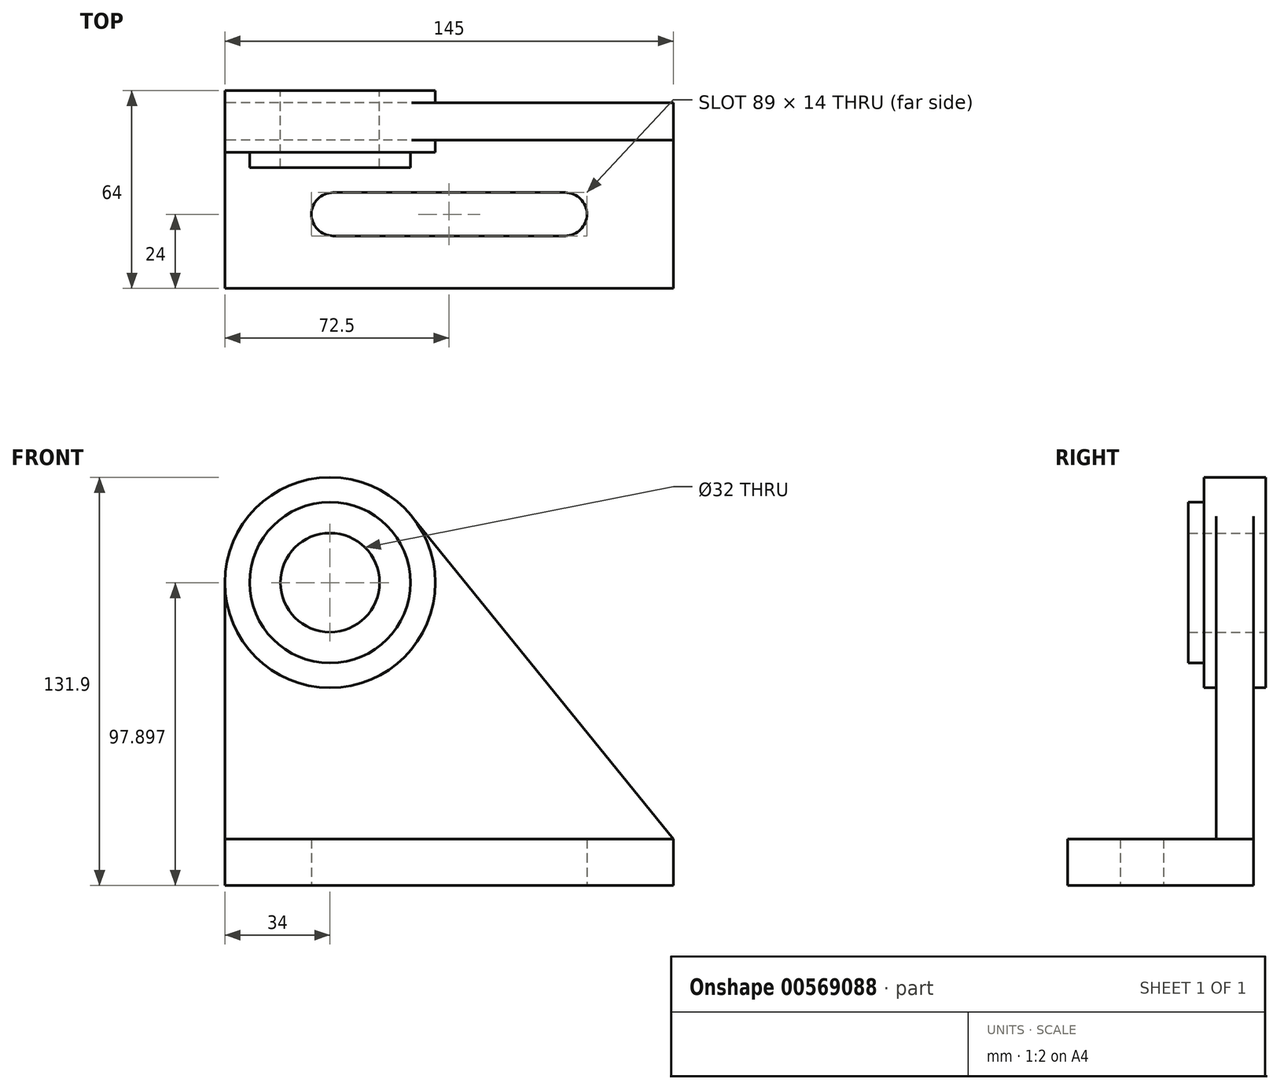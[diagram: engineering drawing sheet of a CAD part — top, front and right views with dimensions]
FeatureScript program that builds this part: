
annotation { "Feature Type Name" : "Feature", "Feature Type Description" : "" }
export const myFeature = defineFeature(function(context is Context, id is Id, definition is map)
    precondition{}
    {
        {
            var Q0;
            Q0=qCreatedBy(makeId("Top.planeOp"),FACE);
            var sketch = newSketch(context, id + "F0", { "sketchPlane" : qUnion([Q0])});
            skLineSegment(sketch, "E0.bottom", {"start": v(-72.5, 30) * mm, "end": v(72.5, 30) * mm});
            skLineSegment(sketch, "E0.top", {"start": v(-72.5, -30) * mm, "end": v(72.5, -30) * mm});
            skLineSegment(sketch, "E0.left", {"start": v(-72.5, 30) * mm, "end": v(-72.5, -30) * mm});
            skLineSegment(sketch, "E0.right", {"start": v(72.5, 30) * mm, "end": v(72.5, -30) * mm});
            skArc(sketch, "E1", {"start": v(37.5, -13) * mm, "mid": v(44.5, -6) * mm, "end": v(37.5, 1) * mm});
            skArc(sketch, "E2", {"start": v(-37.5, 1) * mm, "mid": v(-44.5, -6) * mm, "end": v(-37.5, -13) * mm});
            skLineSegment(sketch, "E3", {"start": v(-37.5, 1) * mm, "end": v(37.5, 1) * mm});
            skLineSegment(sketch, "E4", {"start": v(-37.5, -13) * mm, "end": v(37.5, -13) * mm});
            skSolve(sketch);
        }
        {
            var Q0;
            Q0=qSketchRegion(id+"F0",true);
            extrude(context, id + "F1", {"entities" : qUnion([Q0]), "depth" : 15 * mm});
        }
        {
            var Q0;
            Q0=makeQuery(id+"F1.opExtrude","SWEPT_FACE",FACE,{"disambiguationData":[OSD([sQuery(id+"F0.wireOp",EDGE,"E0.bottom")])]});
            cPlane(context, id + "F2", {"entities" : qUnion([Q0]), "cplaneType" : CPlaneType.OFFSET, "offset" : 0 * mm, "width" : 150 * mm, "height" : 150 * mm});
        }
        {
            var Q0;
            Q0=qCreatedBy(id+"F2.planeOp",FACE);
            var sketch = newSketch(context, id + "F3", { "sketchPlane" : qUnion([Q0])});
            skLineSegment(sketch, "E5.bottom", {"start": v(-72.5, 15) * mm, "end": v(72.5, 15) * mm});
            skLineSegment(sketch, "E5.top", {"start": v(-72.5, 0) * mm, "end": v(72.5, 0) * mm});
            skLineSegment(sketch, "E5.left", {"start": v(-72.5, 15) * mm, "end": v(-72.5, 0) * mm});
            skLineSegment(sketch, "E5.right", {"start": v(72.5, 15) * mm, "end": v(72.5, 0) * mm});
            skLineSegment(sketch, "E6", {"start": v(72.5, 15) * mm, "end": v(72.5, 103.43) * mm});
            skCircle(sketch, "E7", {"center": v(38.5, 97.9) * mm, "radius": 16 * mm});
            skCircle(sketch, "E8", {"center": v(38.5, 97.9) * mm, "radius": 26 * mm});
            skCircle(sketch, "E9", {"center": v(38.5, 97.9) * mm, "radius": 34 * mm});
            skLineSegment(sketch, "E10", {"start": v(-72.5, 15) * mm, "end": v(12.1, 119.31) * mm});
            skSolve(sketch);
        }
        {
            var Q0;
            {var subQ0=sQuery(id+"F3.wireOp",EDGE,"E5.bottom");Q0=makeQuery(id+"F3.imprint","IMPRINT",FACE,{"disambiguationData":[TD([[makeQuery(id+"F3.imprint","IMPRINT",EDGE,{"derivedFrom":subQ0}),1.0]])]});}
            extrude(context, id + "F4", {"entities" : qUnion([Q0]), "operationType" : NewBodyOperationType.ADD, "oppositeDirection" : true, "depth" : 12 * mm});
        }
        {
            var Q0;
            Q0=makeQuery(id+"F3.imprint","IMPRINT",FACE,{"disambiguationData":[TD([[makeQuery(id+"F3.imprint","IMPRINT",EDGE,{"derivedFrom":sQuery(id+"F3.wireOp",EDGE,"E8")}),-1.0]])]});
            extrude(context, id + "F5", {"entities" : qUnion([Q0]), "operationType" : NewBodyOperationType.ADD, "oppositeDirection" : true, "depth" : 16 * mm});
        }
        {
            var Q0;
            Q0=makeQuery(id+"F3.imprint","IMPRINT",FACE,{"disambiguationData":[TD([[makeQuery(id+"F3.imprint","IMPRINT",EDGE,{"derivedFrom":sQuery(id+"F3.wireOp",EDGE,"E7")}),-1.0]])]});
            extrude(context, id + "F6", {"entities" : qUnion([Q0]), "operationType" : NewBodyOperationType.ADD, "oppositeDirection" : true, "depth" : 21 * mm});
        }
        {
            var Q0;
            Q0=makeQuery(id+"F3.imprint","IMPRINT",FACE,{"disambiguationData":[TD([[makeQuery(id+"F3.imprint","IMPRINT",EDGE,{"derivedFrom":sQuery(id+"F3.wireOp",EDGE,"E8")}),-1.0]])]});
            extrude(context, id + "F7", {"entities" : qUnion([Q0]), "operationType" : NewBodyOperationType.ADD, "depth" : 4 * mm});
        }
        {
            var Q0;
            Q0=makeQuery(id+"F3.imprint","IMPRINT",FACE,{"disambiguationData":[TD([[makeQuery(id+"F3.imprint","IMPRINT",EDGE,{"derivedFrom":sQuery(id+"F3.wireOp",EDGE,"E7")}),-1.0]])]});
            extrude(context, id + "F8", {"entities" : qUnion([Q0]), "operationType" : NewBodyOperationType.ADD, "depth" : 4 * mm});
        }
    });
